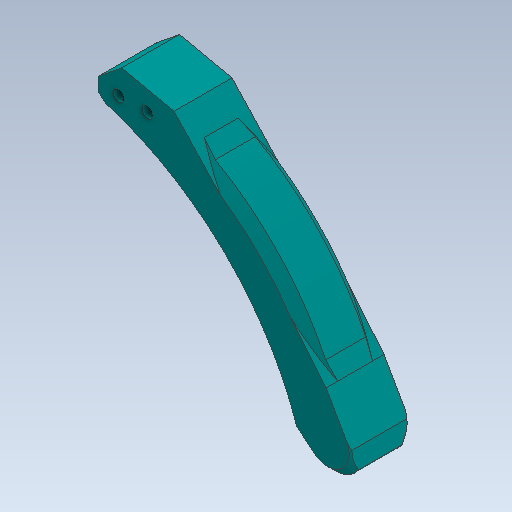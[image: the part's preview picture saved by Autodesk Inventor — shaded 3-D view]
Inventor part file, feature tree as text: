
AUTODESK INVENTOR PART (.ipt)
format: ipt  version: 2020 (Build 240168000, 168)  size: 173,056 bytes
history: native  units: in
note: dims shown in document units (in); Inventor stores cm internally (conversion verified against a paired STEP export)
features: other x3, sketch x2
ambient origin geometry x8: Origin, YZ Plane, XZ Plane, XY Plane, X Axis, Y Axis, Z Axis, Center Point
bodies: Solid1 (feature_tree)
feature tree (5):
  other  "Tarsus.ipt"
  other  "Solid1::Tarsus.ipt"
  other  "TaggingFeature1"
  sketch  "Sketch1"  dims[d0=0.3937in]
  sketch  "Sketch2"
